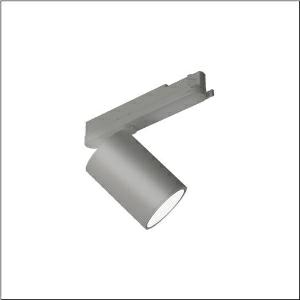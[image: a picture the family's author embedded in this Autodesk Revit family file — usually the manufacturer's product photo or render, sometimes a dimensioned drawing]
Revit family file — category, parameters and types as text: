
# Revit family: spot_31_51sf62mad4b
name_source: partatom
category: Lighting Fixtures
units: mm (PartAtom-declared; Revit-internal decimal feet)

## family parameters
Cut with Voids When Loaded = No
Host = Face
Light Source = No
Part Type = Normal
Room Calculation Point = No
Round Connector Dimension = Use Diameter
Shared = No

## types (1)
- --- (1 x LED, 5140 lm, 41.6 W, 4000K)
    Apparent Load = 42 VA
    CIE Flux Codes = 93 97 99 100 100
    Color Rendering = 90
    Color Temperature = 4000K
    Default Elevation = 1800 mm
    Description = Spot 31, directional spotlight, light control with lens, of PMMA, LED rated luminous flux: 4.930lm, light colour: 940, control gear: ECG Multilumen, with 3-phase adapter, mains connection: 220..240V, AC, 50/60Hz, of aluminium, metallic grey (RAL 9006), length: 213mm, diameter: 90mm, protection rating (complete): IP20, insulation class (complete): insulation class I (protective earthing), certification: CE, impact resistance: IK02, permissible ambient temperature for indoor applications: -20..+40°C, packaging unit: 1 piece
    Height = 175 mm
    Lamp = 1 x LED
    Lamp Light Flux = 5140 lm
    Lamp Power = 41.6 W
    Lamp count = 1
    Length = 90 mm
    Luminous efficacy = 124 lm/W
    Manufacturer = Siteco
    ModVariant = No
    Model = 51SF62MAD4B
    Mounting Place = Ceiling
    Mounting Type = Pendant
    Number of Poles = 1
    OnlyDefault = Yes
    Power Factor = 1
    Product Name = Spot 31
    Product group = directional spotlight
    ProductGroupID = 905
    Protection Class = Protection class I
    Protection Degree = IP 20
    RLX_Detail_Level = 1
    RLX_Emergency_Light_Flux = 0 lm
    RLX_Emergency_Type = 0
    RLX_Emergency_Type_DB = No
    RlxData = <blob elided: 20021 chars, md5=c563ef12>
    Socket = socket
    Standby Power = 0 W
    System Light Flux = 5140 lm
    System Power = 42 W
    Type Comments = factory setting: luminous flux: 100 % | (ON | ON | ON | ON) | 1050 mA
    Type Image = l_1273725.jpg
    URL = http://relux.com
    VarID = @adj_116467
    Voltage = 0 V
    Weight = 0.00 kg
    Width = 0 mm  [stored 0 ft]

note: [stored X ft] marks values corroborated as IEEE doubles in the binary element streams (Revit-internal decimal feet)

## geometry (parser evidence)
native form markers: Blend x4, Sweep x10
no freeform markers — native parametric forms only
